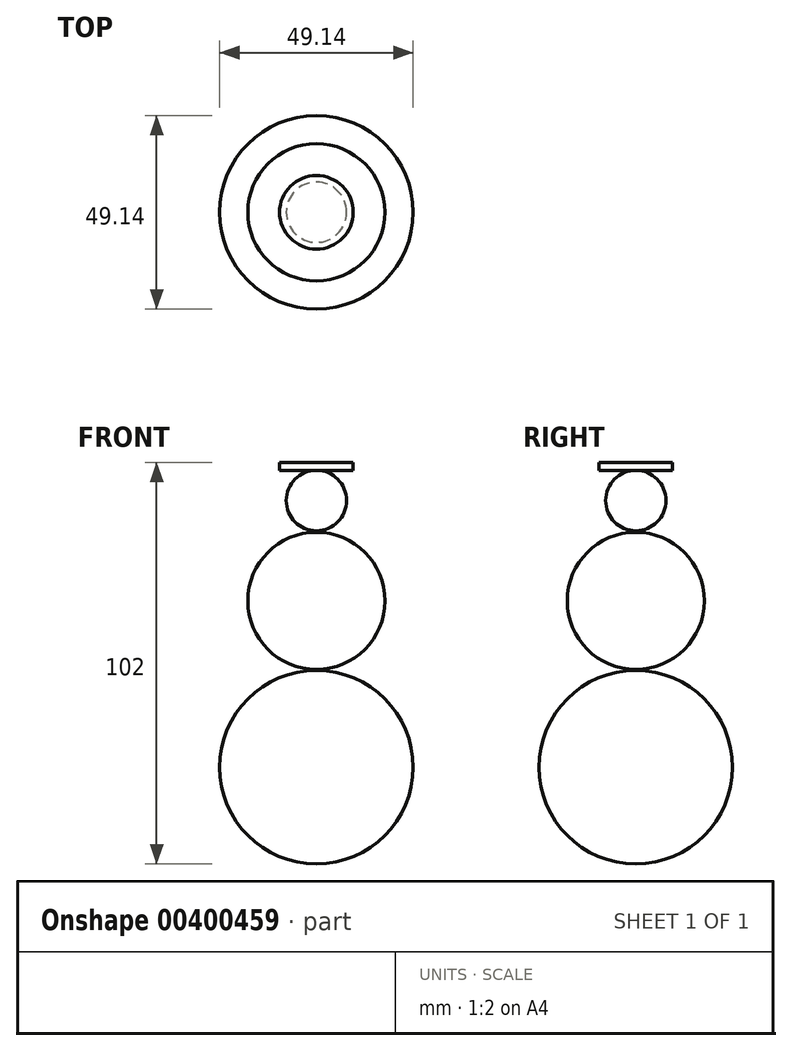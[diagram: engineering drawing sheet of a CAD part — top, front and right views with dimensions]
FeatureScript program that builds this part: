
annotation { "Feature Type Name" : "Feature", "Feature Type Description" : "" }
export const myFeature = defineFeature(function(context is Context, id is Id, definition is map)
    precondition{}
    {
        {
            var Q0;
            Q0=qCreatedBy(makeId("Front.planeOp"),FACE);
            var sketch = newSketch(context, id + "F0", { "sketchPlane" : qUnion([Q0])});
            skCircle(sketch, "E0", {"center": v(0, -32.58) * mm, "radius": 24.57 * mm});
            skCircle(sketch, "E1", {"center": v(0, 9.68) * mm, "radius": 17.42 * mm});
            skCircle(sketch, "E2", {"center": v(0, 35.17) * mm, "radius": 7.67 * mm});
            skLineSegment(sketch, "E3", {"start": v(0, 56.46) * mm, "end": v(0, -66.78) * mm});
            skLineSegment(sketch, "E4.bottom", {"start": v(0, 42.83) * mm, "end": v(-9.36, 42.83) * mm});
            skLineSegment(sketch, "E4.top", {"start": v(0, 44.84) * mm, "end": v(-9.36, 44.84) * mm});
            skLineSegment(sketch, "E4.left", {"start": v(0, 42.83) * mm, "end": v(0, 44.84) * mm});
            skLineSegment(sketch, "E4.right", {"start": v(-9.36, 42.83) * mm, "end": v(-9.36, 44.84) * mm});
            skLineSegment(sketch, "E5.bottom", {"start": v(-4.68, 44.84) * mm, "end": v(0, 44.84) * mm});
            skLineSegment(sketch, "E5.top", {"start": v(-4.68, 56.46) * mm, "end": v(0, 56.46) * mm});
            skLineSegment(sketch, "E5.left", {"start": v(-4.68, 44.84) * mm, "end": v(-4.68, 56.46) * mm});
            skLineSegment(sketch, "E5.right", {"start": v(0, 44.84) * mm, "end": v(0, 56.46) * mm});
            skSolve(sketch);
        }
        {
            var Q0;
            Q0=makeQuery(id+"F0.imprint","IMPRINT",FACE,{"disambiguationData":[TD([[makeQuery(id+"F0.imprint","IMPRINT",EDGE,{"derivedFrom":sQuery(id+"F0.wireOp",EDGE,"E4.bottom")}),-1.0]])]});
            var Q1;
            {var subQ0=sQuery(id+"F0.wireOp",EDGE,"E3");var subQ1=sQuery(id+"F0.wireOp",EDGE,"E2");var subQ3=makeQuery(id+"F0.imprint","INTERSECT",VERTEX,{"derivedFrom":[subQ1,subQ0]});Q1=makeQuery(id+"F0.imprint","IMPRINT",FACE,{"disambiguationData":[TD([[makeQuery(id+"F0.imprint","IMPRINT",EDGE,{"disambiguationData":[TD([[subQ3,1.0]])],"derivedFrom":subQ1}),1.0]])]});}
            var Q2;
            {var subQ0=sQuery(id+"F0.wireOp",EDGE,"E3");var subQ1=sQuery(id+"F0.wireOp",EDGE,"E1");var subQ2=makeQuery(id+"F0.imprint","INTERSECT",VERTEX,{"disambiguationData":[OD(0.0)],"derivedFrom":[subQ1,subQ0]});Q2=makeQuery(id+"F0.imprint","IMPRINT",FACE,{"disambiguationData":[TD([[makeQuery(id+"F0.imprint","IMPRINT",EDGE,{"disambiguationData":[TD([[subQ2,1.0]])],"derivedFrom":subQ1}),1.0]])]});}
            var Q3;
            {var subQ0=sQuery(id+"F0.wireOp",EDGE,"E3");var subQ1=sQuery(id+"F0.wireOp",EDGE,"E0");var subQ2=makeQuery(id+"F0.imprint","INTERSECT",VERTEX,{"disambiguationData":[OD(0.0)],"derivedFrom":[subQ1,subQ0]});Q3=makeQuery(id+"F0.imprint","IMPRINT",FACE,{"disambiguationData":[TD([[makeQuery(id+"F0.imprint","IMPRINT",EDGE,{"disambiguationData":[TD([[subQ2,1.0]])],"derivedFrom":subQ1}),1.0]])]});}
            var Q4;
            Q4=makeQuery(id+"F0.imprint","IMPRINT",FACE,{"disambiguationData":[TD([[makeQuery(id+"F0.imprint","IMPRINT",EDGE,{"derivedFrom":sQuery(id+"F0.wireOp",EDGE,"E5.bottom")}),1.0]])]});
            var Q5;
            Q5=sQuery(id+"F0.wireOp",EDGE,"E3");
            revolve(context, id + "F1", {"entities" : qUnion([Q0, Q1, Q2, Q3, Q4]), "axis" : qUnion([Q5]), "revolveType" : RevolveType.FULL});
        }
    });
